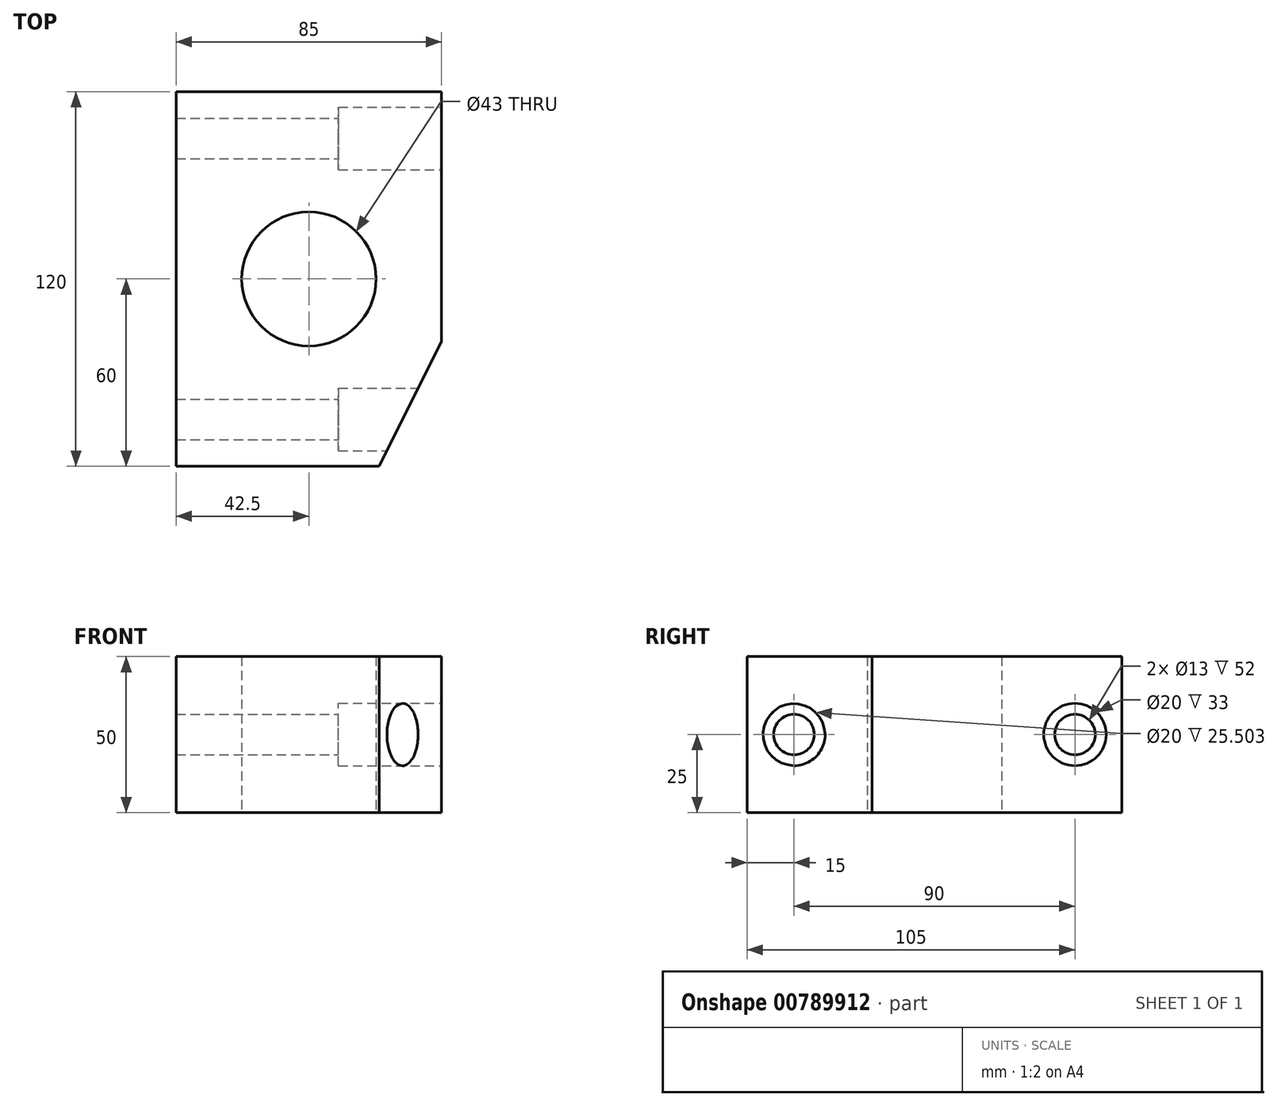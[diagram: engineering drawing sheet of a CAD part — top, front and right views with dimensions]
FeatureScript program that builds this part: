
annotation { "Feature Type Name" : "Feature", "Feature Type Description" : "" }
export const myFeature = defineFeature(function(context is Context, id is Id, definition is map)
    precondition{}
    {
        {
            var Q0;
            Q0=qCreatedBy(makeId("Top.planeOp"),FACE);
            var sketch = newSketch(context, id + "F0", { "sketchPlane" : qUnion([Q0])});
            skLineSegment(sketch, "E0.bottom", {"start": v(-42.5, 60) * mm, "end": v(42.5, 60) * mm});
            skLineSegment(sketch, "E0.top", {"start": v(-42.5, -60) * mm, "end": v(22.5, -60) * mm});
            skLineSegment(sketch, "E0.left", {"start": v(-42.5, 60) * mm, "end": v(-42.5, -60) * mm});
            skLineSegment(sketch, "E0.right", {"start": v(42.5, 60) * mm, "end": v(42.5, -20) * mm});
            skPoint(sketch, "E0.middle", {"position": v(0, 0) * mm});
            skLineSegment(sketch, "E1", {"start": v(42.5, -20) * mm, "end": v(22.5, -60) * mm});
            skCircle(sketch, "E2", {"center": v(0, 0) * mm, "radius": 21.5 * mm});
            skSolve(sketch);
        }
        {
            var Q0;
            Q0=qSketchRegion(id+"F0",true);
            extrude(context, id + "F1", {"entities" : qUnion([Q0]), "depth" : 50 * mm, "offsetDistance" : 25 * mm});
        }
        {
            var Q0;
            Q0=makeQuery(id+"F1.opExtrude","SWEPT_FACE",FACE,{"disambiguationData":[OSD([sQuery(id+"F0.wireOp",EDGE,"E0.right")])]});
            var sketch = newSketch(context, id + "F2", { "sketchPlane" : qUnion([Q0])});
            skLineSegment(sketch, "E3.0.0", {"start": v(-20, 0) * mm, "end": v(60, 0) * mm, "construction": true});
            skLineSegment(sketch, "E3.0.1", {"start": v(60, 0) * mm, "end": v(60, 50) * mm, "construction": true});
            skLineSegment(sketch, "E3.0.2", {"start": v(60, 50) * mm, "end": v(-20, 50) * mm, "construction": true});
            skLineSegment(sketch, "E4.0", {"start": v(-20, 50) * mm, "end": v(-60, 50) * mm, "construction": true});
            skLineSegment(sketch, "E5.0", {"start": v(-60, 50) * mm, "end": v(-60, 0) * mm, "construction": true});
            skLineSegment(sketch, "E6.0", {"start": v(-20, 0) * mm, "end": v(-60, 0) * mm, "construction": true});
            skCircle(sketch, "E7", {"center": v(45, 25) * mm, "radius": 10 * mm});
            skCircle(sketch, "E8", {"center": v(-45, 25) * mm, "radius": 10 * mm});
            skSolve(sketch);
        }
        {
            var Q0;
            Q0=qSketchRegion(id+"F2",true);
            extrude(context, id + "F3", {"entities" : qUnion([Q0]), "operationType" : NewBodyOperationType.REMOVE, "oppositeDirection" : true, "depth" : 33 * mm, "offsetDistance" : 25 * mm});
        }
        {
            var Q0;
            Q0=qCreatedBy(makeId("Right.planeOp"),FACE);
            var sketch = newSketch(context, id + "F4", { "sketchPlane" : qUnion([Q0])});
            skPoint(sketch, "E9.0", {"position": v(-45, 25) * mm});
            skPoint(sketch, "E10.0", {"position": v(45, 25) * mm});
            skCircle(sketch, "E11", {"center": v(-45, 25) * mm, "radius": 6.5 * mm});
            skCircle(sketch, "E12", {"center": v(45, 25) * mm, "radius": 6.5 * mm});
            skSolve(sketch);
        }
        {
            var Q0;
            Q0=qSketchRegion(id+"F4",true);
            extrude(context, id + "F5", {"entities" : qUnion([Q0]), "operationType" : NewBodyOperationType.REMOVE, "endBound" : BoundingType.UP_TO_NEXT, "oppositeDirection" : true, "depth" : 25 * mm, "offsetDistance" : 25 * mm, "hasSecondDirection" : true, "secondDirectionBound" : BoundingType.UP_TO_NEXT, "secondDirectionOppositeDirection" : false, "secondDirectionDepth" : 25 * mm});
        }
    });
